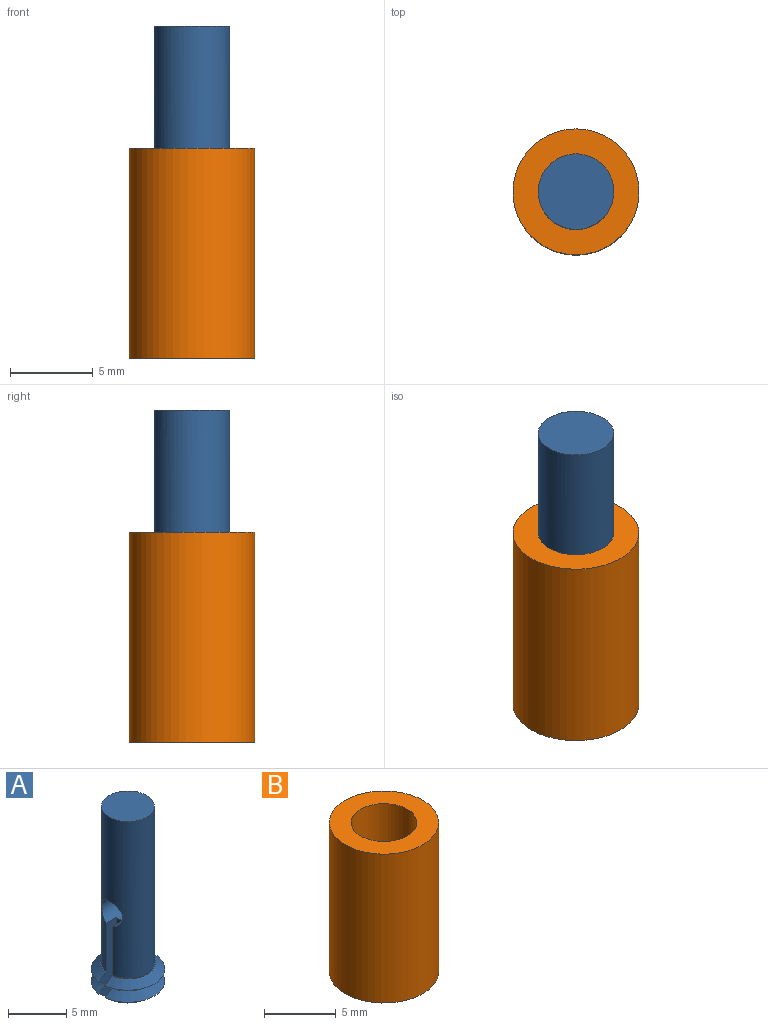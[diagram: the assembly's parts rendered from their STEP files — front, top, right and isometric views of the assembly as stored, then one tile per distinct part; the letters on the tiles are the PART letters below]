
ASSEMBLY  parts=2 mates=1
PART A: 23 faces, bbox 6.3x6.4x19.1 mm
  f0: cone r=3.17mm half-angle=51.3deg, axis (0,0,1), area 8.1mm2, adj f1,f13,f17,f20
  f1: cone r=2.38mm half-angle=51.3deg, axis (0,0,-1), area 8.1mm2, adj f0,f2,f17,f20
  f2: cone r=3.17mm half-angle=51.3deg, axis (0,0,1), area 8.1mm2, adj f1,f3,f17,f20
  f3: cone r=2.38mm half-angle=51.3deg, axis (0,0,-1), area 8.1mm2, adj f2,f4,f17,f20
  f4: plane 4.7x2mm, normal (0,0,1), area 0.6mm2, adj f3,f6,f17,f20
  f5: cylinder r=1.27mm len=2.54mm, axis (-1,0,0), area 17.8mm2, adj f6,f19,f20,f21,f22
  f6: cylinder r=2.29mm len=16.51mm, axis (0,0,-1), area 222.2mm2, adj f4,f5,f11,f12,f14,f16,f17,f20
  f7: cone r=3.17mm half-angle=51.3deg, axis (0,0,1), area 8.1mm2, adj f8,f13,f16,f21
  f8: cone r=2.38mm half-angle=51.3deg, axis (0,0,-1), area 8.1mm2, adj f7,f9,f16,f21
  f9: cone r=3.17mm half-angle=51.3deg, axis (0,0,1), area 8.1mm2, adj f8,f10,f16,f21
  f10: cone r=2.38mm half-angle=51.3deg, axis (0,0,-1), area 8.1mm2, adj f9,f11,f16,f21
  f11: plane 4.7x2mm, normal (0,0,1), area 0.6mm2, adj f6,f10,f16,f21
  f12: plane 4.57x4.57mm, normal (0,0,1), area 16.4mm2, adj f6
  f13: plane 4.77x4.7mm, normal (0,0,-1), area 15.8mm2, adj f0,f7,f16,f17,f18,f20,f21,f22
  f14: cylinder r=1.27mm len=2.54mm, axis (1,0,0), area 17.8mm2, adj f6,f15,f16,f17,f18
  f15: plane 2.54x2.54mm, normal (1,0,0), area 5.1mm2, adj f14
  f16: plane 3.25x2.15mm, normal (0,1,0), area 5.3mm2, adj f6,f7,f8,f9,f10,f11,f13,f14
  f17: plane 3.25x2.15mm, normal (0,-1,0), area 5.3mm2, adj f0,f1,f2,f3,f4,f6,f13,f14
  f18: plane 3.23x0.76mm, normal (1,0,0), area 2.4mm2, adj f13,f14,f16,f17
  f19: plane 2.54x2.54mm, normal (-1,0,0), area 5.1mm2, adj f5
  f20: plane 7.69x2.15mm, normal (0,-1,0), area 10.8mm2, adj f0,f1,f2,f3,f4,f5,f6,f13
  f21: plane 7.69x2.15mm, normal (0,1,0), area 10.8mm2, adj f5,f6,f7,f8,f9,f10,f11,f13
  f22: plane 7.68x0.76mm, normal (-1,0,0), area 5.8mm2, adj f5,f13,f20,f21
PART B: 9 faces, bbox 7.6x7.6x12.7 mm
  f0: cone r=2.38mm half-angle=51.3deg, axis (0,0,-1), area 17.7mm2, adj f1,f8
  f1: cone r=3.17mm half-angle=51.3deg, axis (0,0,1), area 17.7mm2, adj f0,f2
  f2: plane 7.62x7.62mm, normal (0,0,-1), area 27.8mm2, adj f1,f3
  f3: cylinder r=3.81mm len=12.7mm, axis (0,0,-1), area 304mm2, adj f2,f4
  f4: plane 7.62x7.62mm, normal (0,0,1), area 29.2mm2, adj f3,f5
  f5: cylinder r=2.29mm len=10.16mm, axis (0,0,-1), area 145.9mm2, adj f4,f6
  f6: plane 4.77x4.77mm, normal (0,0,-1), area 1.4mm2, adj f5,f7
  f7: cone r=2.38mm half-angle=51.3deg, axis (0,0,-1), area 17.7mm2, adj f6,f8
  f8: cone r=3.17mm half-angle=51.3deg, axis (0,0,1), area 17.7mm2, adj f0,f7
PLACE A at identity fixed
PLACE B rot(axis=(0,0,-1),90deg) t=(0,0,-1.03)mm
MATE slider B.f0 <-> A.f0  axis (0,0,-1) through (0,0,5.32)mm
